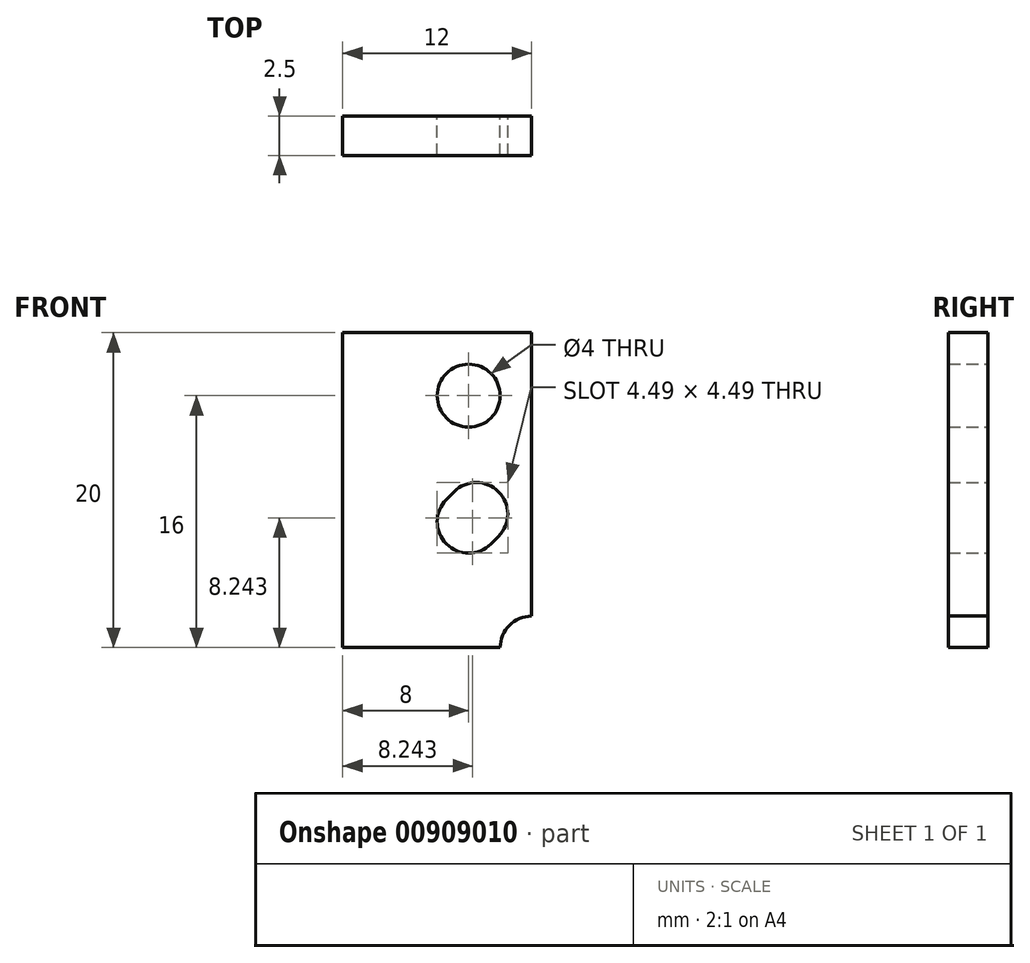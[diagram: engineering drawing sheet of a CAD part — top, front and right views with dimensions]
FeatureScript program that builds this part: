
annotation { "Feature Type Name" : "Feature", "Feature Type Description" : "" }
export const myFeature = defineFeature(function(context is Context, id is Id, definition is map)
    precondition{}
    {
        {
            var Q0;
            Q0=qCreatedBy(makeId("Front.planeOp"),FACE);
            var sketch = newSketch(context, id + "F0", { "sketchPlane" : qUnion([Q0])});
            skLineSegment(sketch, "E0.bottom", {"start": v(0, 0) * mm, "end": v(10, 0) * mm});
            skLineSegment(sketch, "E0.top", {"start": v(0, 20) * mm, "end": v(12, 20) * mm});
            skLineSegment(sketch, "E0.left", {"start": v(0, 0) * mm, "end": v(0, 20) * mm});
            skLineSegment(sketch, "E0.right", {"start": v(12, 2) * mm, "end": v(12, 20) * mm});
            skCircle(sketch, "E1", {"center": v(8, 16) * mm, "radius": 2 * mm});
            skLineSegment(sketch, "E2.bottom", {"start": v(0, 0) * mm, "end": v(8, 0) * mm, "construction": true});
            skLineSegment(sketch, "E2.top", {"start": v(0, 8) * mm, "end": v(8, 8) * mm, "construction": true});
            skLineSegment(sketch, "E2.left", {"start": v(0, 0) * mm, "end": v(0, 8) * mm, "construction": true});
            skLineSegment(sketch, "E2.right", {"start": v(8, 0) * mm, "end": v(8, 8) * mm, "construction": true});
            skLineSegment(sketch, "E3", {"start": v(8, 8) * mm, "end": v(0, 0) * mm, "construction": true});
            skArc(sketch, "E4", {"start": v(6.59, 9.41) * mm, "mid": v(6.59, 6.59) * mm, "end": v(9.41, 6.59) * mm});
            skArc(sketch, "E5", {"start": v(9.9, 7.07) * mm, "mid": v(9.9, 9.9) * mm, "end": v(7.07, 9.9) * mm});
            skLineSegment(sketch, "E6", {"start": v(7.07, 9.9) * mm, "end": v(6.59, 9.41) * mm});
            skLineSegment(sketch, "E7", {"start": v(9.9, 7.07) * mm, "end": v(9.41, 6.59) * mm});
            skArc(sketch, "E8", {"start": v(12, 2) * mm, "mid": v(10.59, 1.41) * mm, "end": v(10, 0) * mm});
            skSolve(sketch);
        }
        {
            var Q0;
            Q0 = qSketchRegion(id + "F0", true);
            extrude(context, id + "F1", {"entities" : qUnion([Q0]), "depth" : 2.5 * mm, "offsetDistance" : 25 * mm});
        }
    });
